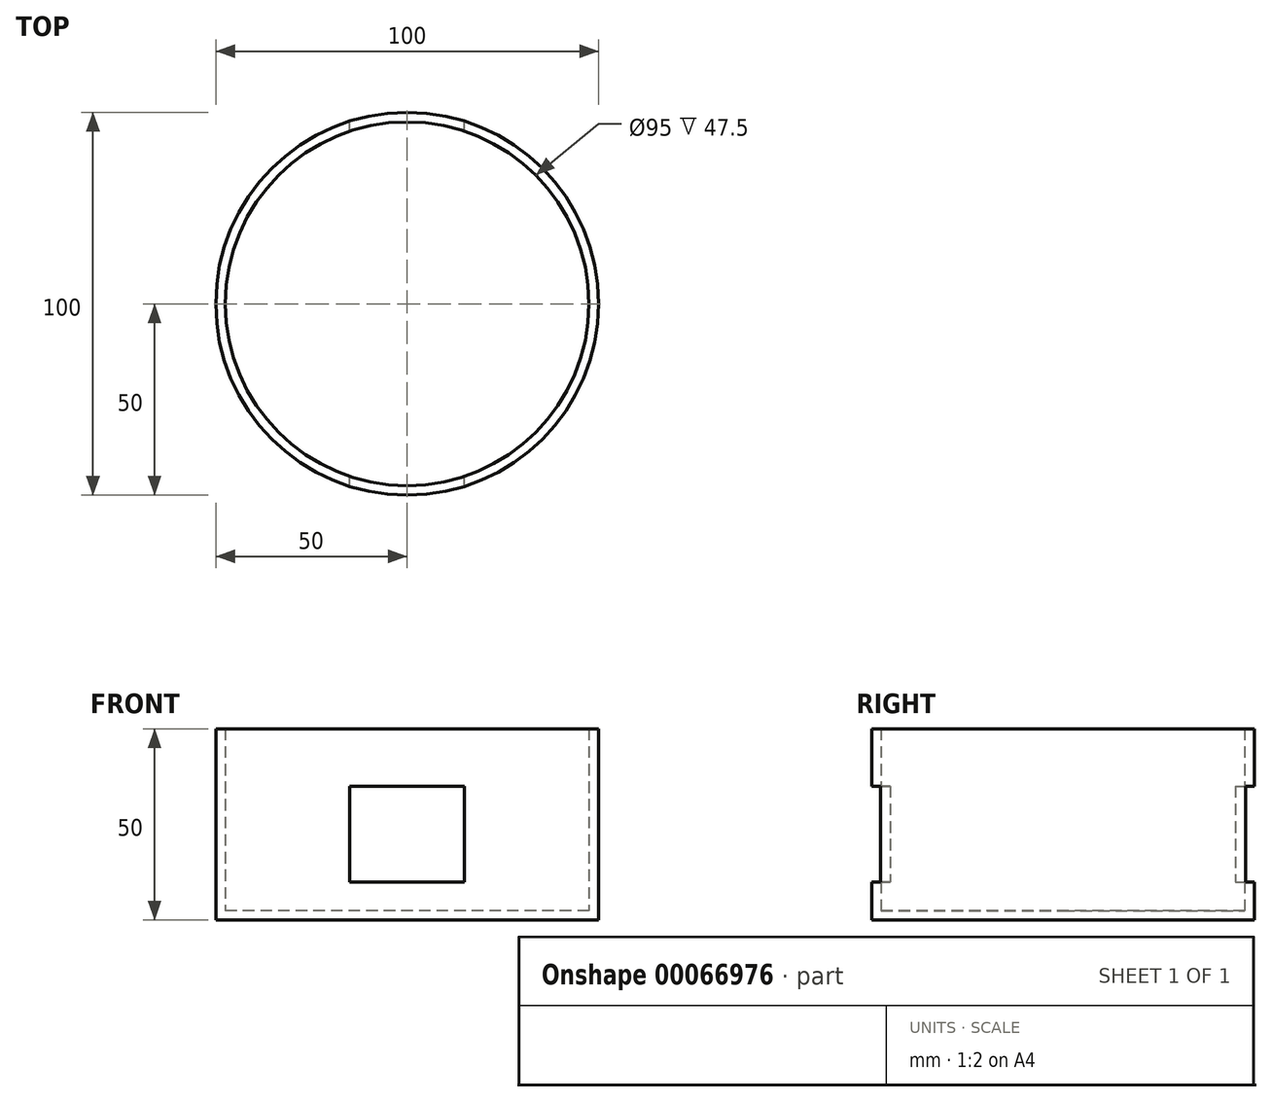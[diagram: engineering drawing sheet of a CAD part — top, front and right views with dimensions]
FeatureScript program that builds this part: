
annotation { "Feature Type Name" : "Feature", "Feature Type Description" : "" }
export const myFeature = defineFeature(function(context is Context, id is Id, definition is map)
    precondition{}
    {
        {
            var Q0;
            Q0=qCreatedBy(makeId("Top.planeOp"),FACE);
            var sketch = newSketch(context, id + "F0", { "sketchPlane" : qUnion([Q0])});
            skCircle(sketch, "E0", {"center": v(0, 0) * mm, "radius": 50 * mm});
            skSolve(sketch);
        }
        {
            var Q0;
            Q0 = qSketchRegion(id + "F0", true);
            extrude(context, id + "F1", {"entities" : qUnion([Q0]), "depth" : 50 * mm});
        }
        {
            var Q0;
            Q0=makeQuery(id+"F1.opExtrude","CAP_FACE",FACE,{"disambiguationData":[OSD([sQuery(id+"F0.wireOp",EDGE,"E0")])],"isStart":false});
            shell(context, id + "F2", {"entities" : qUnion([Q0]), "thickness" : 2.5 * mm});
        }
        {
            var Q0;
            Q0=qCreatedBy(makeId("Front.planeOp"),FACE);
            var sketch = newSketch(context, id + "F3", { "sketchPlane" : qUnion([Q0])});
            skLineSegment(sketch, "E1.bottom", {"start": v(-15, 35) * mm, "end": v(15, 35) * mm});
            skLineSegment(sketch, "E1.top", {"start": v(-15, 10) * mm, "end": v(15, 10) * mm});
            skLineSegment(sketch, "E1.left", {"start": v(-15, 35) * mm, "end": v(-15, 10) * mm});
            skLineSegment(sketch, "E1.right", {"start": v(15, 35) * mm, "end": v(15, 10) * mm});
            skLineSegment(sketch, "E2", {"start": v(0, 0) * mm, "end": v(0, 10) * mm, "construction": true});
            skSolve(sketch);
        }
        {
            var Q0;
            Q0 = qSketchRegion(id + "F3", true);
            extrude(context, id + "F4", {"entities" : qUnion([Q0]), "operationType" : NewBodyOperationType.REMOVE, "endBound" : BoundingType.THROUGH_ALL, "depth" : 25 * mm, "hasSecondDirection" : true, "secondDirectionBound" : SecondDirectionBoundingType.THROUGH_ALL, "secondDirectionOppositeDirection" : true, "secondDirectionDepth" : 25 * mm});
        }
    });
